# Revit family: RN 26000 Rubinetto a sfera per caldaie
name_source: partatom
category: Rohrzubehör
units: mm (PartAtom-declared; Revit-internal decimal feet)

## family parameters
Arbeitsebenenbasiert = Nein
Beim Laden mit Abzugskörper schneiden = Nein
Bemaßung runder Anschluss = Durchmesser verwenden
Gemeinsam genutzt = Nein
Immer vertikal = Ja
Teiletyp = Ventil - Zerlegung in

## types (3) — shared parameters
1.010.00.2 Number of the part of the guideline = 2
1.010.00.3 Issue date (month) of the guideline = 201601
1.010.00.4 Manufacturer name = R. Nussbaum AG
1.010.00.5 Revision date of the file = 20190514
1.100.00.3 Sort number for display sequence = 4
1.100.00.4 Product designation = Absperr- und Regelarmaturen
1.960/3L.00.8 Link (URL) = https://www.nussbaum.ch
2.700.00.4 valve assembly type = 11
2.700.00.7 maximum operating temperature TB [°C] = 100
2.700.00.8 maximum operating pressure(working pressure) ps [1.0 · 102 Pa] = 16
Connector Visibility = Nein
EnclosingSpace Visibility = Nein
Hersteller = R. Nussbauzm AG
Modell = 0
URL = https://www.nussbaum.ch

## per-type parameters (varying)
| type | 1.800.00.3 BS number | 1.810.00.3 Manufacturer’s reference number | 1.810.00.4 DATANORM number | 1.810.00.5 StLB number | 1.810.00.6 GTIN number | 2.700.00.26 product description | 2.700.00.5 nominal size DN | 2.700.00.6 kvs-value [m3/h] | CONNECTOR0_DIAMETER_dX_0r | CONNECTOR0_dX_00 | CONNECTOR0_dX_01 | CONNECTOR0_ref_dX | R. Nussbaum AG 26000.54 en Visibility | R. Nussbaum AG 26000.55 en Visibility | R. Nussbaum AG 26000.56 en Visibility | Typenkommentare |
| DN 15 | 0040010000000000000000000000010010000000000000000100000000 | 26000.54 | 26000.54 | 635.103 | 7612945675927 | 26000.54, Kessel-Kugelhahn, mit Aussengewinde, DN=15, R=½ | 15 | 16.3 | 15 mm  [stored 0.0492126 ft] | 39 mm | 24 mm | 24 mm | Ja | Nein | Nein | Valvola d'arrestoDN 15 |
| DN 20 | 0040010000000000000000000000010010000000000000000200000000 | 26000.55 | 26000.55 | 635.104 | 7612945676115 | 26000.55, Kessel-Kugelhahn, mit Aussengewinde, DN=20, R=¾ | 20 | 29.5 | 20 mm | 45 mm | 28 mm | 28 mm | Nein | Ja | Nein | Valvola d'arrestoDN 20 |
| DN 25 | 0040010000000000000000000000010010000000000000000300000000 | 26000.56 | 26000.56 | 635.105 | 7612945676139 | 26000.56, Kessel-Kugelhahn, mit Aussengewinde, DN=25, R=1 | 25 | 43 | 25 mm  [stored 0.082021 ft] | 50 mm | 31 mm | 31 mm | Nein | Nein | Ja | Valvola d'arrestoDN 25 |

note: [stored X ft] marks values corroborated as IEEE doubles in the binary element streams (Revit-internal decimal feet)

## geometry (parser evidence)
native form markers: Sweep x2
no freeform markers — native parametric forms only
